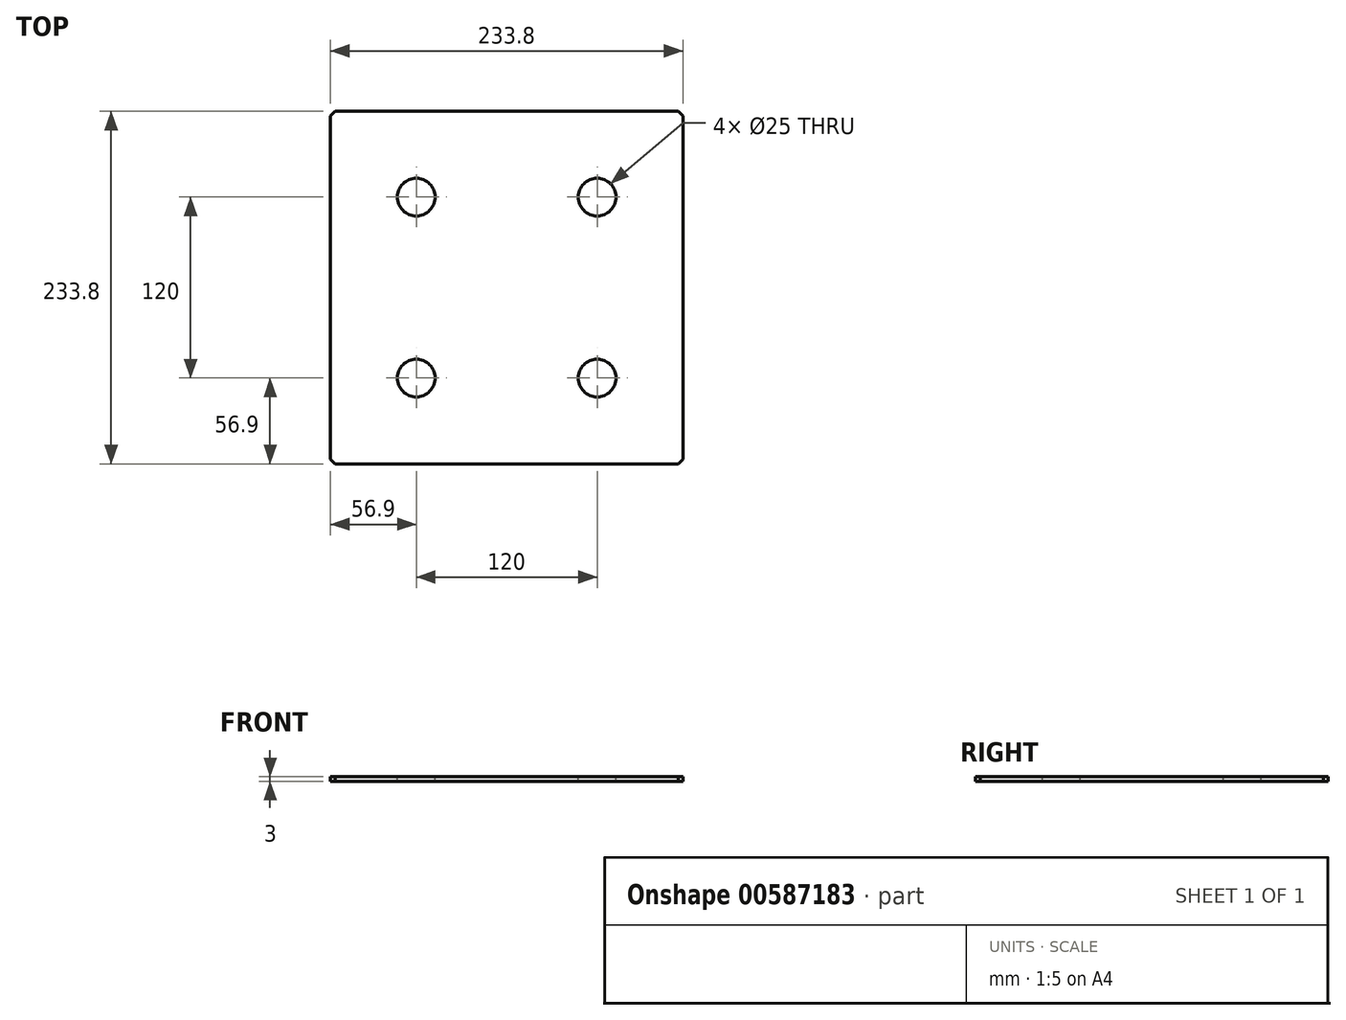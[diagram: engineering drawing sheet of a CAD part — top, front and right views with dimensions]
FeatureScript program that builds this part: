
annotation { "Feature Type Name" : "Feature", "Feature Type Description" : "" }
export const myFeature = defineFeature(function(context is Context, id is Id, definition is map)
    precondition{}
    {
        {
            var Q0;
            Q0=qCreatedBy(makeId("Top.planeOp"),FACE);
            var sketch = newSketch(context, id + "F0", { "sketchPlane" : qUnion([Q0])});
            skLineSegment(sketch, "E0.bottom", {"start": v(-116.9, 116.9) * mm, "end": v(116.9, 116.9) * mm});
            skLineSegment(sketch, "E0.top", {"start": v(-116.9, -116.9) * mm, "end": v(116.9, -116.9) * mm});
            skLineSegment(sketch, "E0.left", {"start": v(-116.9, 116.9) * mm, "end": v(-116.9, -116.9) * mm});
            skLineSegment(sketch, "E0.right", {"start": v(116.9, 116.9) * mm, "end": v(116.9, -116.9) * mm});
            skPoint(sketch, "E0.middle", {"position": v(0, 0) * mm});
            skSolve(sketch);
        }
        {
            var Q0;
            Q0 = qSketchRegion(id + "F0", true);
            extrude(context, id + "F1", {"entities" : qUnion([Q0]), "depth" : 3 * mm, "offsetDistance" : 25 * mm});
        }
        {
            var Q0;
            Q0=makeQuery(id+"F1.opExtrude","CAP_FACE",FACE,{"disambiguationData":[OSD([sQuery(id+"F0.wireOp",EDGE,"E0.bottom"),sQuery(id+"F0.wireOp",EDGE,"E0.top"),sQuery(id+"F0.wireOp",EDGE,"E0.left"),sQuery(id+"F0.wireOp",EDGE,"E0.right")])],"isStart":false});
            var sketch = newSketch(context, id + "F2", { "sketchPlane" : qUnion([Q0])});
            skCircle(sketch, "E1", {"center": v(-60, 60) * mm, "radius": 12.5 * mm});
            skCircle(sketch, "E2.MirrorC", {"center": v(-60, -60) * mm, "radius": 12.5 * mm});
            skCircle(sketch, "E3.MirrorC", {"center": v(60, -60) * mm, "radius": 12.5 * mm});
            skCircle(sketch, "E4.MirrorC", {"center": v(60, 60) * mm, "radius": 12.5 * mm});
            skSolve(sketch);
        }
        {
            var Q0;
            Q0 = qSketchRegion(id + "F2", true);
            extrude(context, id + "F3", {"entities" : qUnion([Q0]), "operationType" : NewBodyOperationType.REMOVE, "endBound" : BoundingType.THROUGH_ALL, "oppositeDirection" : true, "depth" : 25 * mm, "offsetDistance" : 25 * mm});
        }
        {
            var Q0;
            Q0=makeQuery(id+"F1.opExtrude","SWEPT_EDGE",EDGE,{"disambiguationData":[OSD([sQuery(id+"F0.wireOp",EDGE,"E0.bottom"),sQuery(id+"F0.wireOp",EDGE,"E0.right")])]});
            var Q1;
            Q1=makeQuery(id+"F1.opExtrude","SWEPT_EDGE",EDGE,{"disambiguationData":[OSD([sQuery(id+"F0.wireOp",EDGE,"E0.bottom"),sQuery(id+"F0.wireOp",EDGE,"E0.left")])]});
            var Q2;
            Q2=makeQuery(id+"F1.opExtrude","SWEPT_EDGE",EDGE,{"disambiguationData":[OSD([sQuery(id+"F0.wireOp",EDGE,"E0.top"),sQuery(id+"F0.wireOp",EDGE,"E0.right")])]});
            var Q3;
            Q3=makeQuery(id+"F1.opExtrude","SWEPT_EDGE",EDGE,{"disambiguationData":[OSD([sQuery(id+"F0.wireOp",EDGE,"E0.top"),sQuery(id+"F0.wireOp",EDGE,"E0.left")])]});
            chamfer(context, id + "F4", {"entities" : qUnion([Q0, Q1, Q2, Q3]), "width" : 3 * mm, "tangentPropagation" : true});
        }
    });
